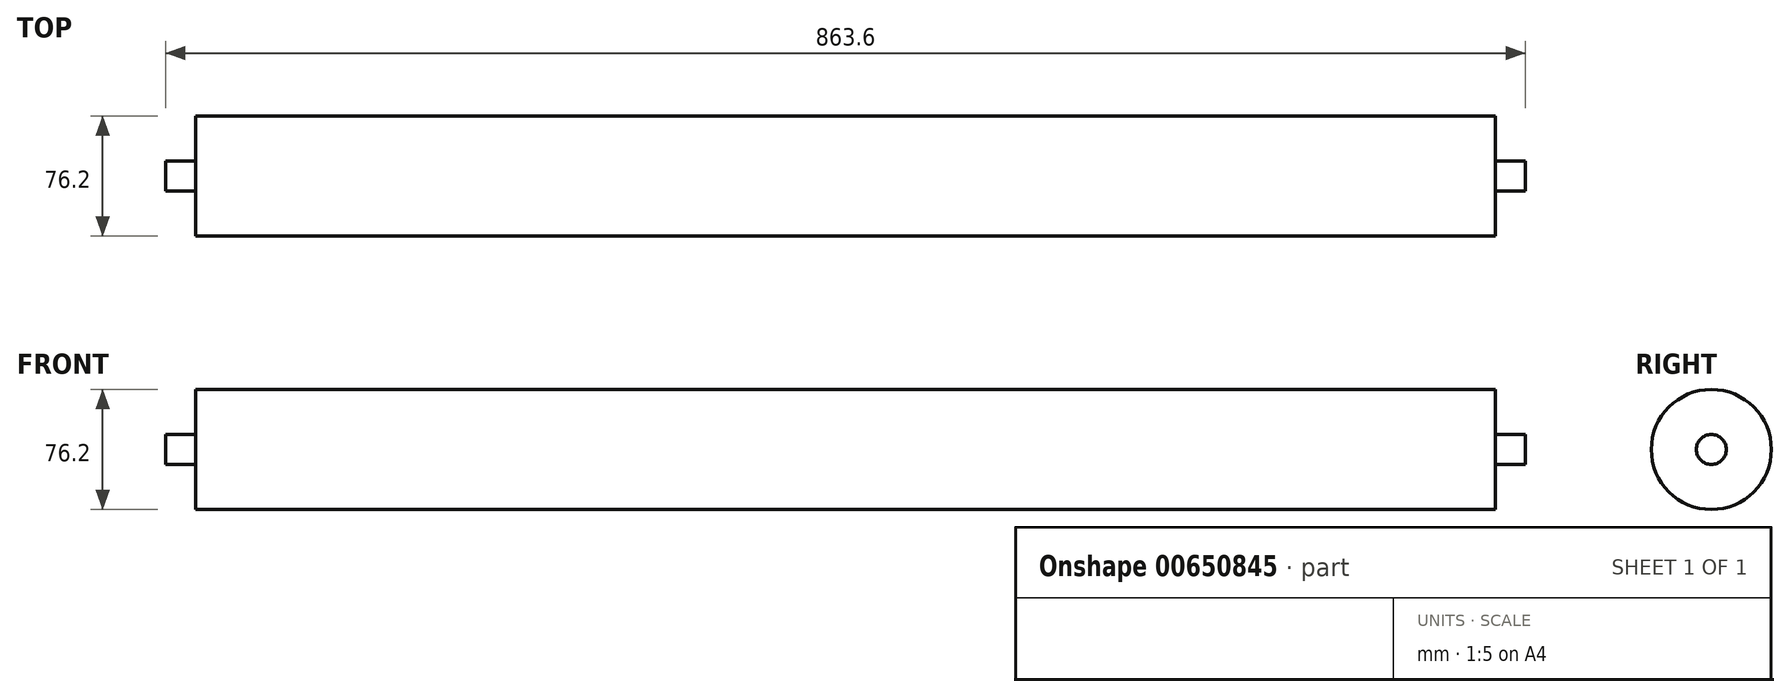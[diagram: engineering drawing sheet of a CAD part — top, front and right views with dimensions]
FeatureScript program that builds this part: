
annotation { "Feature Type Name" : "Feature", "Feature Type Description" : "" }
export const myFeature = defineFeature(function(context is Context, id is Id, definition is map)
    precondition{}
    {
        {
            var Q0;
            Q0=qCreatedBy(makeId("Right.planeOp"),FACE);
            var sketch = newSketch(context, id + "F0", { "sketchPlane" : qUnion([Q0])});
            skCircle(sketch, "E0", {"center": v(0, 0) * mm, "radius": 9.53 * mm});
            skSolve(sketch);
        }
        {
            var Q0;
            Q0 = qSketchRegion(id + "F0", true);
            extrude(context, id + "F1", {"entities" : qUnion([Q0]), "oppositeDirection" : true, "depth" : 19.05 * mm, "offsetDistance" : 25.4 * mm});
        }
        {
            var Q0;
            Q0=makeQuery(id+"F1.opExtrude","CAP_FACE",FACE,{"disambiguationData":[OSD([sQuery(id+"F0.wireOp",EDGE,"E0")])],"isStart":false});
            var sketch = newSketch(context, id + "F2", { "sketchPlane" : qUnion([Q0])});
            skCircle(sketch, "E1", {"center": v(0, 0) * mm, "radius": 38.1 * mm});
            skSolve(sketch);
        }
        {
            var Q0;
            Q0 = qSketchRegion(id + "F2", true);
            extrude(context, id + "F3", {"entities" : qUnion([Q0]), "operationType" : NewBodyOperationType.ADD, "depth" : 825.5 * mm, "offsetDistance" : 25.4 * mm});
        }
        {
            var Q0;
            Q0=makeQuery(id+"F3.opExtrude","CAP_FACE",FACE,{"disambiguationData":[OSD([sQuery(id+"F2.wireOp",EDGE,"E1")])],"isStart":false});
            var sketch = newSketch(context, id + "F4", { "sketchPlane" : qUnion([Q0])});
            skCircle(sketch, "E2", {"center": v(0, 0) * mm, "radius": 9.53 * mm});
            skSolve(sketch);
        }
        {
            var Q0;
            Q0 = qSketchRegion(id + "F4", true);
            extrude(context, id + "F5", {"entities" : qUnion([Q0]), "operationType" : NewBodyOperationType.ADD, "depth" : 19.05 * mm, "offsetDistance" : 25.4 * mm});
        }
    });
